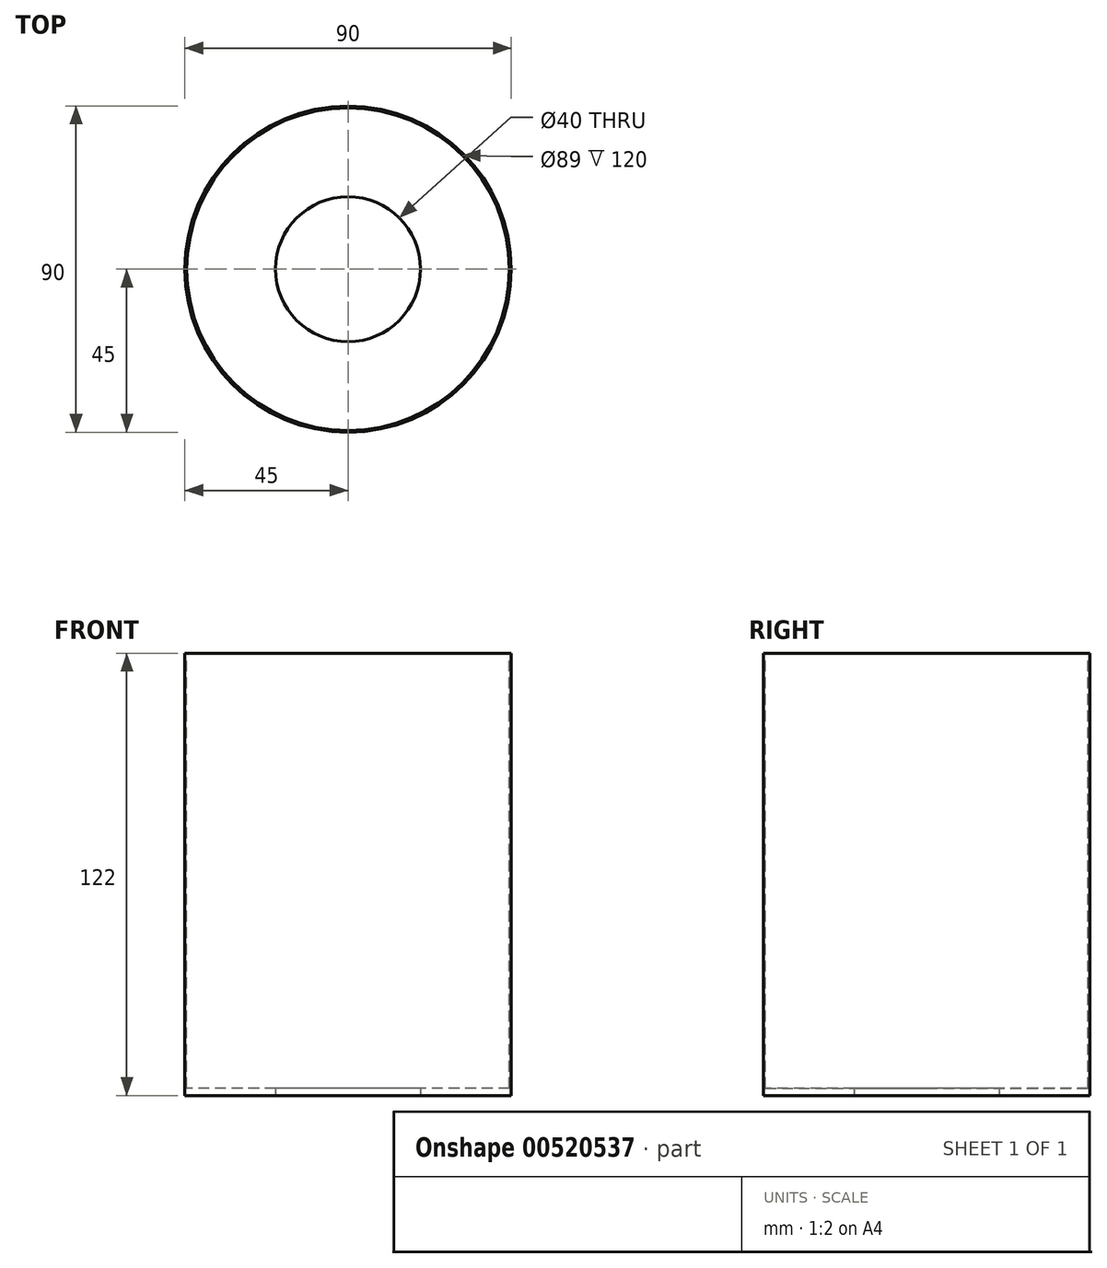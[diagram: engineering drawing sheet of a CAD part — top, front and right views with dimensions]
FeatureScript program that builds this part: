
annotation { "Feature Type Name" : "Feature", "Feature Type Description" : "" }
export const myFeature = defineFeature(function(context is Context, id is Id, definition is map)
    precondition{}
    {
        {
            var Q0;
            Q0=qCreatedBy(makeId("Top.planeOp"),FACE);
            var sketch = newSketch(context, id + "F0", { "sketchPlane" : qUnion([Q0])});
            skCircle(sketch, "E0", {"center": v(0, 0) * mm, "radius": 45 * mm});
            skCircle(sketch, "E1", {"center": v(0, 0) * mm, "radius": 20 * mm});
            skSolve(sketch);
        }
        {
            var Q0;
            Q0=makeQuery(id+"F0.imprint","IMPRINT",FACE,{"disambiguationData":[TD([[makeQuery(id+"F0.imprint","IMPRINT",EDGE,{"derivedFrom":sQuery(id+"F0.wireOp",EDGE,"E0")}),1.0]])]});
            extrude(context, id + "F1", {"entities" : qUnion([Q0]), "depth" : 2 * mm, "offsetDistance" : 25 * mm});
        }
        {
            var Q0;
            Q0=makeQuery(id+"F1.opExtrude","CAP_FACE",FACE,{"disambiguationData":[OSD([sQuery(id+"F0.wireOp",EDGE,"E0")])],"isStart":false});
            extrude(context, id + "F2", {"entities" : qUnion([Q0]), "operationType" : NewBodyOperationType.ADD, "depth" : 120 * mm, "offsetDistance" : 25 * mm});
        }
        {
            var Q0;
            Q0=makeQuery(id+"F2.opExtrude","CAP_FACE",FACE,{"disambiguationData":[OSD([sQuery(id+"F0.wireOp",EDGE,"E0")])],"isStart":false});
            var sketch = newSketch(context, id + "F3", { "sketchPlane" : qUnion([Q0])});
            skCircle(sketch, "E2", {"center": v(0, 0) * mm, "radius": 45.3 * mm});
            skCircle(sketch, "E3", {"center": v(0, 0) * mm, "radius": 44.5 * mm});
            skSolve(sketch);
        }
        {
            var Q0;
            Q0=makeQuery(id+"F3.imprint","IMPRINT",FACE,{"disambiguationData":[TD([[makeQuery(id+"F3.imprint","IMPRINT",EDGE,{"derivedFrom":sQuery(id+"F3.wireOp",EDGE,"E3")}),1.0]])]});
            extrude(context, id + "F4", {"entities" : qUnion([Q0]), "operationType" : NewBodyOperationType.REMOVE, "oppositeDirection" : true, "depth" : 120 * mm, "offsetDistance" : 25 * mm});
        }
    });
